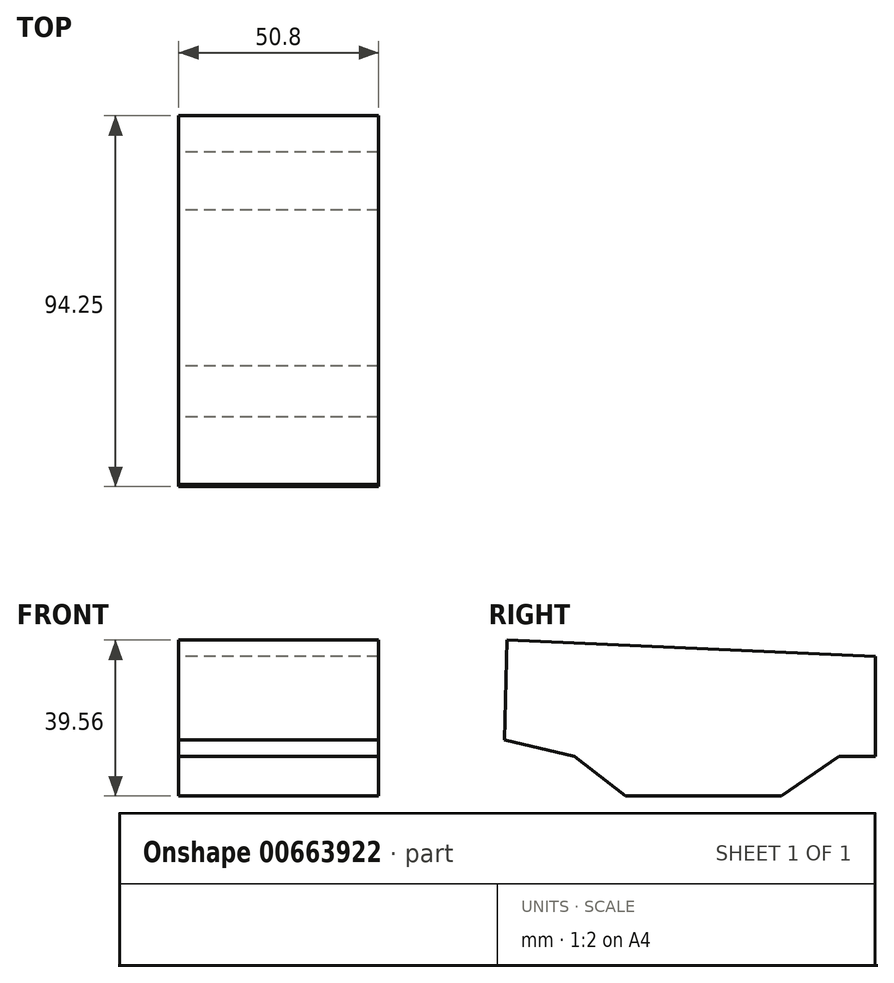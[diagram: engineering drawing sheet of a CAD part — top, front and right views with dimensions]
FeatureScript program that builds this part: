
annotation { "Feature Type Name" : "Feature", "Feature Type Description" : "" }
export const myFeature = defineFeature(function(context is Context, id is Id, definition is map)
    precondition{}
    {
        {
            var Q0;
            Q0=qCreatedBy(makeId("Right.planeOp"),FACE);
            var sketch = newSketch(context, id + "F0", { "sketchPlane" : qUnion([Q0])});
            skLineSegment(sketch, "E0", {"start": v(-134.02, 12.4) * mm, "end": v(-116.27, 8.21) * mm});
            skLineSegment(sketch, "E1", {"start": v(-116.27, 8.21) * mm, "end": v(-103.35, -1.86) * mm});
            skLineSegment(sketch, "E2", {"start": v(-103.35, -1.86) * mm, "end": v(-63.72, -1.86) * mm});
            skLineSegment(sketch, "E3", {"start": v(-63.72, -1.86) * mm, "end": v(-49.06, 8.21) * mm});
            skLineSegment(sketch, "E4", {"start": v(-49.06, 8.21) * mm, "end": v(-39.77, 8.21) * mm});
            skLineSegment(sketch, "E5", {"start": v(-39.77, 8.21) * mm, "end": v(-39.77, 33.55) * mm});
            skLineSegment(sketch, "E6", {"start": v(-39.77, 33.55) * mm, "end": v(-133.44, 37.7) * mm});
            skLineSegment(sketch, "E7", {"start": v(-133.44, 37.7) * mm, "end": v(-134.02, 12.4) * mm});
            skSolve(sketch);
        }
        {
            var Q0;
            Q0 = qSketchRegion(id + "F0", true);
            extrude(context, id + "F1", {"entities" : qUnion([Q0]), "depth" : 25.4 * mm, "offsetDistance" : 25.4 * mm});
        }
        {
            var Q0;
            Q0=makeQuery(id+"F1.opExtrude","CAP_FACE",FACE,{"disambiguationData":[OSD([sQuery(id+"F0.wireOp",EDGE,"E0"),sQuery(id+"F0.wireOp",EDGE,"E1"),sQuery(id+"F0.wireOp",EDGE,"E2"),sQuery(id+"F0.wireOp",EDGE,"E3"),sQuery(id+"F0.wireOp",EDGE,"E4"),sQuery(id+"F0.wireOp",EDGE,"E5"),sQuery(id+"F0.wireOp",EDGE,"E6"),sQuery(id+"F0.wireOp",EDGE,"E7")])],"isStart":true});
            extrude(context, id + "F2", {"entities" : qUnion([Q0]), "operationType" : NewBodyOperationType.ADD, "depth" : 25.4 * mm, "offsetDistance" : 25.4 * mm});
        }
    });
